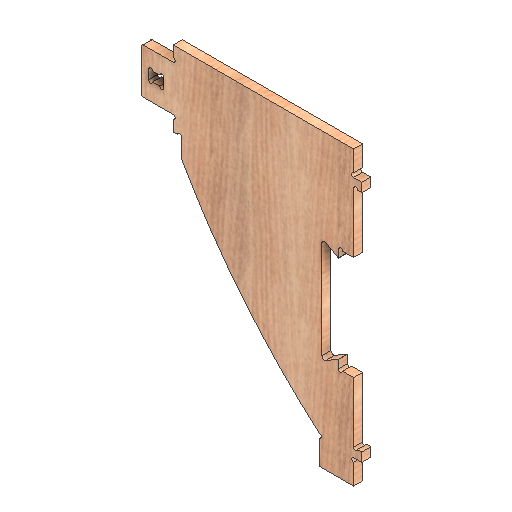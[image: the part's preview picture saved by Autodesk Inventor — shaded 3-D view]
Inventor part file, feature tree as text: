
AUTODESK INVENTOR PART (.ipt)
format: ipt  version: 2021 (Build 250183000, 183)  size: 265,728 bytes
history: native  units: mm
features: other x2, extrude x2, hole x1
ambient origin geometry x8: Origin, YZ Plane, XZ Plane, XY Plane, X Axis, Y Axis, Z Axis, Center Point
bodies: Body1 (feature_tree)
feature tree (5):
  other  "CONTOURS"
  hole  "HOLES"  [1 undecoded]
  other  "LETTERS"
  extrude  "Extrusion3"  Depth=18.0mm TaperAngle=0.0deg
  extrude  "Extrusion4"  [1 undecoded]
note: 2 required parameter values undecoded (feature->parameter linkage not recoverable at this tier; creation-order binding heuristic only, values carry confidence <= 0.55)
